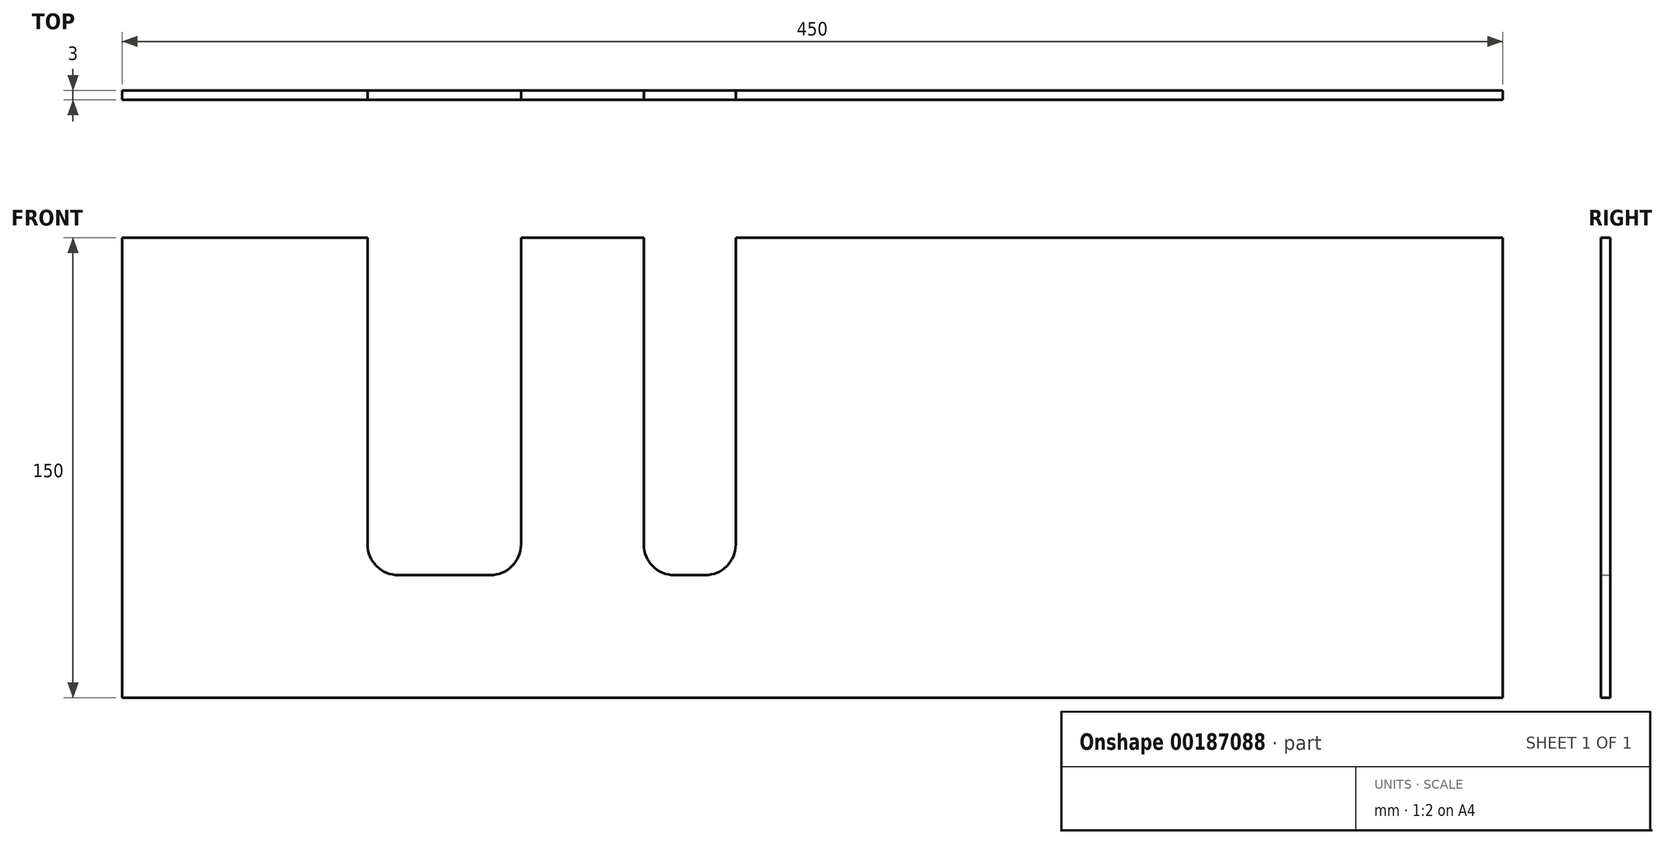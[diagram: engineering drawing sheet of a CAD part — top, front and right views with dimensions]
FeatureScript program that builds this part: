
annotation { "Feature Type Name" : "Feature", "Feature Type Description" : "" }
export const myFeature = defineFeature(function(context is Context, id is Id, definition is map)
    precondition{}
    {
        {
            var Q0;
            Q0=qCreatedBy(makeId("Front.planeOp"),FACE);
            var sketch = newSketch(context, id + "F0", { "sketchPlane" : qUnion([Q0])});
            skLineSegment(sketch, "E0.top", {"start": v(-225, -75) * mm, "end": v(225, -75) * mm});
            skLineSegment(sketch, "E0.left", {"start": v(-225, 75) * mm, "end": v(-225, -75) * mm});
            skLineSegment(sketch, "E0.right", {"start": v(225, 75) * mm, "end": v(225, -75) * mm});
            skLineSegment(sketch, "E1", {"start": v(-225, 75) * mm, "end": v(-145, 75) * mm});
            skLineSegment(sketch, "E2", {"start": v(-145, 75) * mm, "end": v(-145, -35) * mm});
            skLineSegment(sketch, "E3", {"start": v(-145, -35) * mm, "end": v(-95, -35) * mm});
            skLineSegment(sketch, "E4", {"start": v(-95, -35) * mm, "end": v(-95, 75) * mm});
            skLineSegment(sketch, "E5", {"start": v(-95, 75) * mm, "end": v(-55, 75) * mm});
            skLineSegment(sketch, "E6", {"start": v(-55, 75) * mm, "end": v(-55, -35) * mm});
            skLineSegment(sketch, "E7", {"start": v(-55, -35) * mm, "end": v(-25, -35) * mm});
            skLineSegment(sketch, "E8", {"start": v(-25, -35) * mm, "end": v(-25, 75) * mm});
            skLineSegment(sketch, "E9", {"start": v(-25, 75) * mm, "end": v(225, 75) * mm});
            skSolve(sketch);
        }
        {
            var Q0;
            Q0=makeQuery(id+"F0.imprint","IMPRINT",FACE,{"disambiguationData":[TD([[makeQuery(id+"F0.imprint","IMPRINT",EDGE,{"derivedFrom":sQuery(id+"F0.wireOp",EDGE,"E0.top")}),1.0]])]});
            extrude(context, id + "F1", {"entities" : qUnion([Q0]), "depth" : 3 * mm});
        }
        {
            var Q0;
            Q0=makeQuery(id+"F1.opExtrude","SWEPT_EDGE",EDGE,{"disambiguationData":[OSD([sQuery(id+"F0.wireOp",EDGE,"E2"),sQuery(id+"F0.wireOp",EDGE,"E3")])]});
            var Q1;
            Q1=makeQuery(id+"F1.opExtrude","SWEPT_EDGE",EDGE,{"disambiguationData":[OSD([sQuery(id+"F0.wireOp",EDGE,"E3"),sQuery(id+"F0.wireOp",EDGE,"E4")])]});
            var Q2;
            Q2=makeQuery(id+"F1.opExtrude","SWEPT_EDGE",EDGE,{"disambiguationData":[OSD([sQuery(id+"F0.wireOp",EDGE,"E7"),sQuery(id+"F0.wireOp",EDGE,"E8")])]});
            var Q3;
            Q3=makeQuery(id+"F1.opExtrude","SWEPT_EDGE",EDGE,{"disambiguationData":[OSD([sQuery(id+"F0.wireOp",EDGE,"E6"),sQuery(id+"F0.wireOp",EDGE,"E7")])]});
            fillet(context, id + "F2", {"entities" : qUnion([Q0, Q1, Q2, Q3]), "radius" : 10 * mm, "tangentPropagation" : true, "allowEdgeOverflow" : false});
        }
    });
